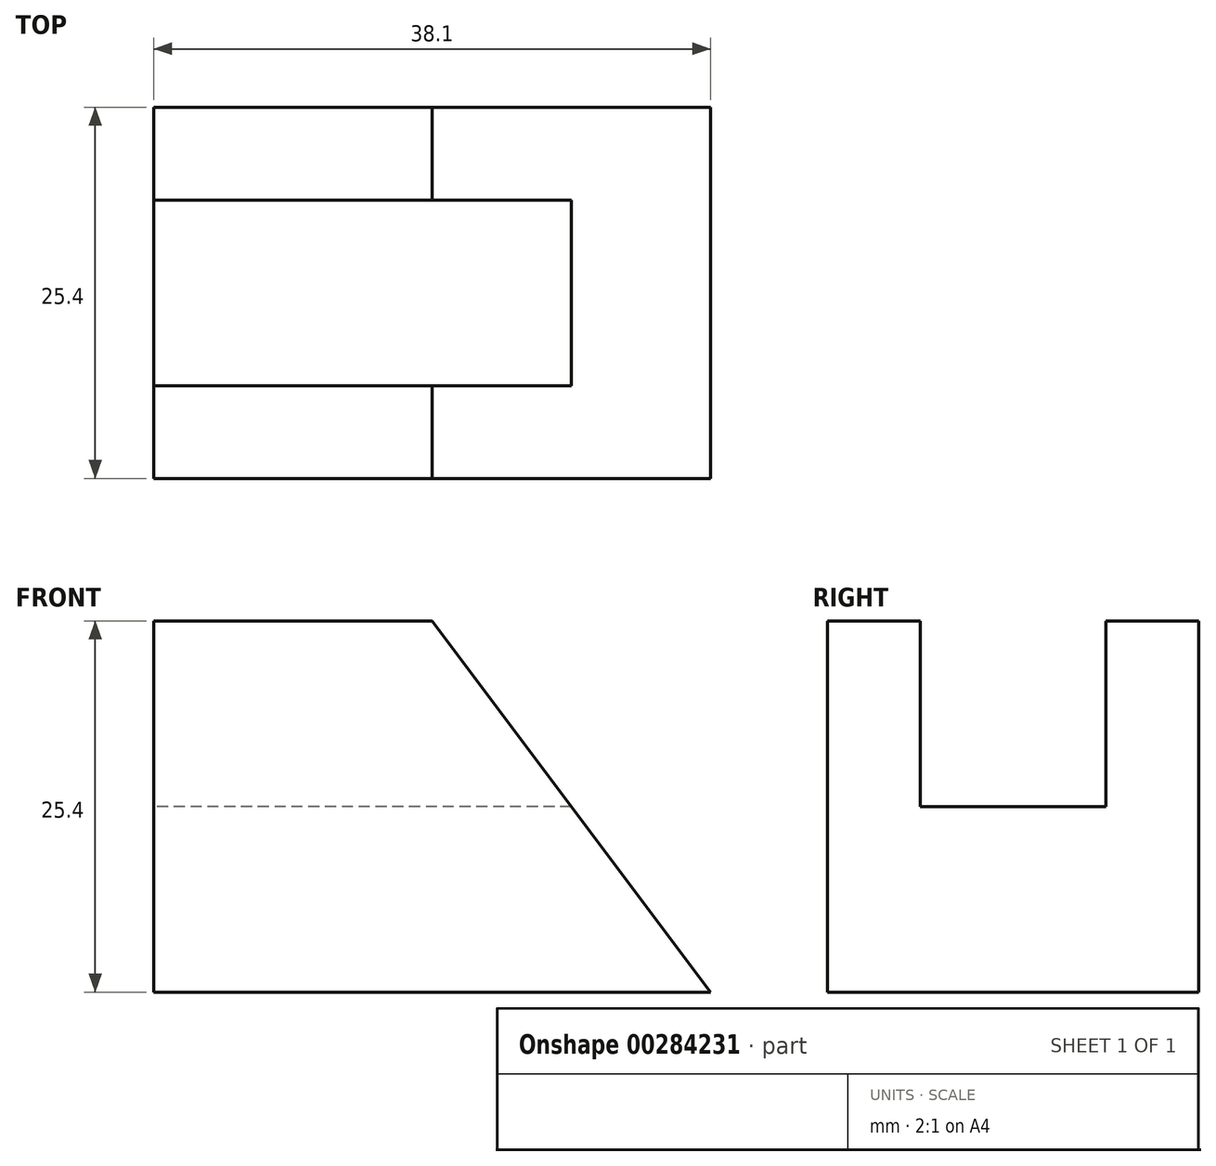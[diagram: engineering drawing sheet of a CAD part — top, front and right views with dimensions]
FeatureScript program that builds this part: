
annotation { "Feature Type Name" : "Feature", "Feature Type Description" : "" }
export const myFeature = defineFeature(function(context is Context, id is Id, definition is map)
    precondition{}
    {
        {
            var Q0;
            Q0=qCreatedBy(makeId("Front.planeOp"),FACE);
            var sketch = newSketch(context, id + "F0", { "sketchPlane" : qUnion([Q0])});
            skLineSegment(sketch, "E0", {"start": v(0, 0) * mm, "end": v(0, 25.4) * mm});
            skLineSegment(sketch, "E1", {"start": v(0, 25.4) * mm, "end": v(19.05, 25.4) * mm});
            skLineSegment(sketch, "E2", {"start": v(19.05, 25.4) * mm, "end": v(38.1, 0) * mm});
            skLineSegment(sketch, "E3", {"start": v(38.1, 0) * mm, "end": v(0, 0) * mm});
            skSolve(sketch);
        }
        {
            var Q0;
            Q0 = qSketchRegion(id + "F0", true);
            extrude(context, id + "F1", {"entities" : qUnion([Q0]), "depth" : 25.4 * mm});
        }
        {
            var Q0;
            Q0=makeQuery(id+"F1.opExtrude","SWEPT_FACE",FACE,{"disambiguationData":[OSD([sQuery(id+"F0.wireOp",EDGE,"E0")])]});
            var sketch = newSketch(context, id + "F2", { "sketchPlane" : qUnion([Q0])});
            skLineSegment(sketch, "E4.bottom", {"start": v(6.35, 25.4) * mm, "end": v(19.05, 25.4) * mm});
            skLineSegment(sketch, "E4.top", {"start": v(6.35, 12.7) * mm, "end": v(19.05, 12.7) * mm});
            skLineSegment(sketch, "E4.left", {"start": v(6.35, 25.4) * mm, "end": v(6.35, 12.7) * mm});
            skLineSegment(sketch, "E4.right", {"start": v(19.05, 25.4) * mm, "end": v(19.05, 12.7) * mm});
            skSolve(sketch);
        }
        {
            var Q0;
            Q0 = qSketchRegion(id + "F2", true);
            extrude(context, id + "F3", {"entities" : qUnion([Q0]), "operationType" : NewBodyOperationType.REMOVE, "endBound" : BoundingType.THROUGH_ALL, "oppositeDirection" : true, "depth" : 25.4 * mm});
        }
    });
